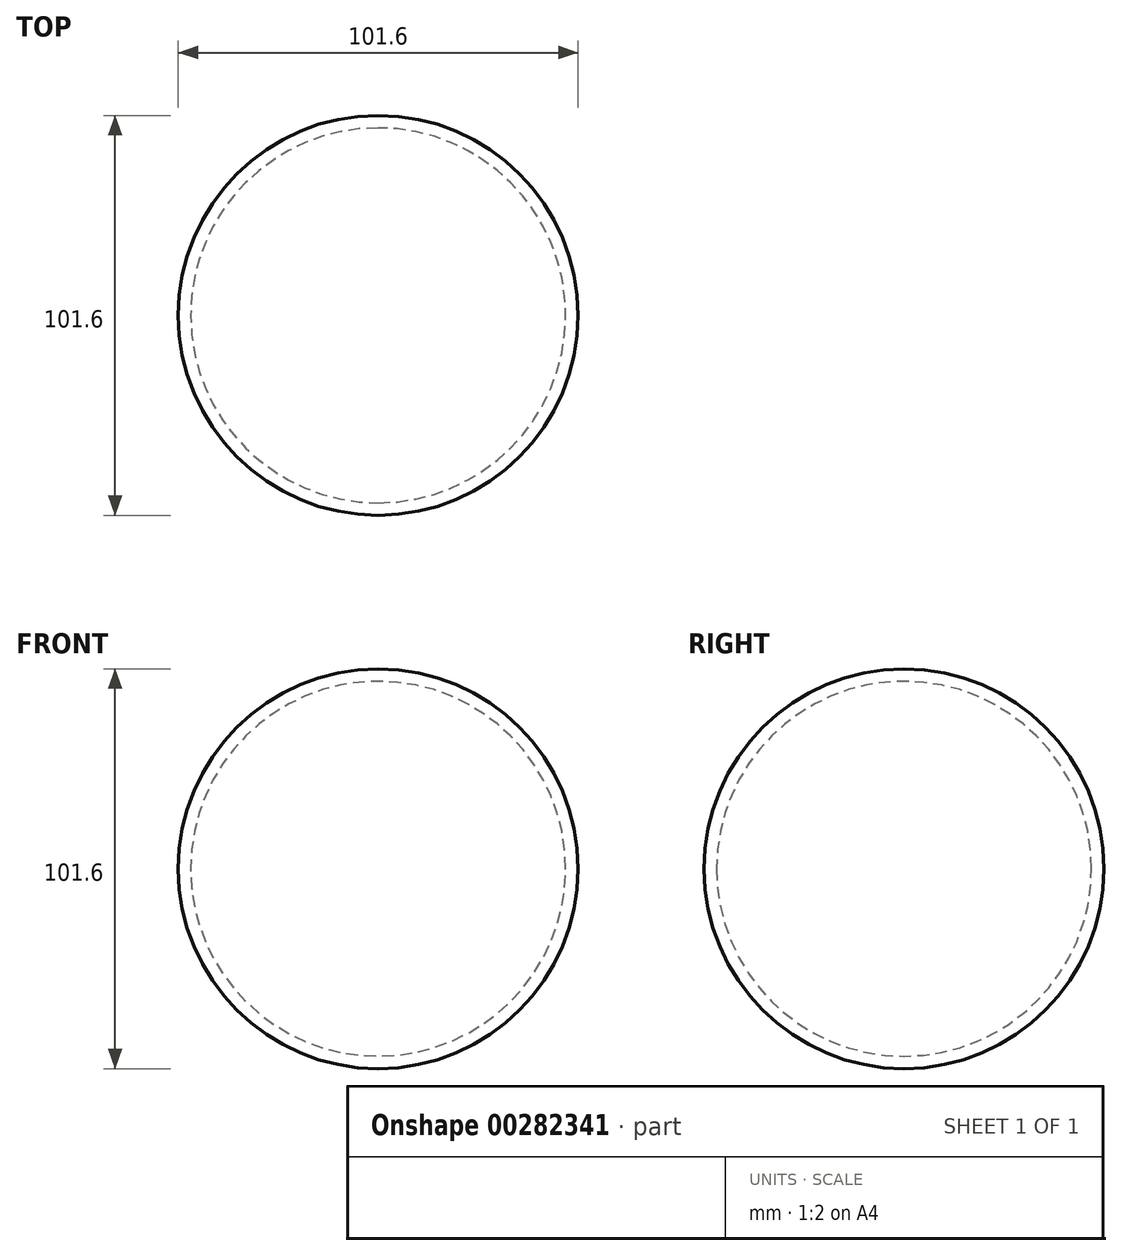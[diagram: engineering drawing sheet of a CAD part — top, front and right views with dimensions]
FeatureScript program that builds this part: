
annotation { "Feature Type Name" : "Feature", "Feature Type Description" : "" }
export const myFeature = defineFeature(function(context is Context, id is Id, definition is map)
    precondition{}
    {
        {
            var Q0;
            Q0=qCreatedBy(makeId("Top.planeOp"),FACE);
            var sketch = newSketch(context, id + "F0", { "sketchPlane" : qUnion([Q0])});
            skArc(sketch, "E0", {"start": v(0, -47.63) * mm, "mid": v(47.63, 0) * mm, "end": v(0, 47.63) * mm});
            skArc(sketch, "E1", {"start": v(0, -50.8) * mm, "mid": v(50.8, 0) * mm, "end": v(0, 50.8) * mm});
            skLineSegment(sketch, "E2", {"start": v(0, 50.8) * mm, "end": v(0, 47.63) * mm});
            skLineSegment(sketch, "E3", {"start": v(0, -50.8) * mm, "end": v(0, -47.63) * mm});
            skLineSegment(sketch, "E4", {"start": v(0, -47.63) * mm, "end": v(0, 0) * mm, "construction": true});
            skLineSegment(sketch, "E5", {"start": v(0, 0) * mm, "end": v(0, 47.63) * mm, "construction": true});
            skSolve(sketch);
        }
        {
            var Q0;
            Q0=makeQuery(id+"F0.imprint","IMPRINT",FACE,{"disambiguationData":[TD([[makeQuery(id+"F0.imprint","IMPRINT",EDGE,{"derivedFrom":sQuery(id+"F0.wireOp",EDGE,"E0")}),-1.0]])]});
            var Q1;
            Q1=sQuery(id+"F0.wireOp",EDGE,"E5");
            revolve(context, id + "F1", {"entities" : qUnion([Q0]), "axis" : qUnion([Q1]), "revolveType" : RevolveType.FULL});
        }
    });
